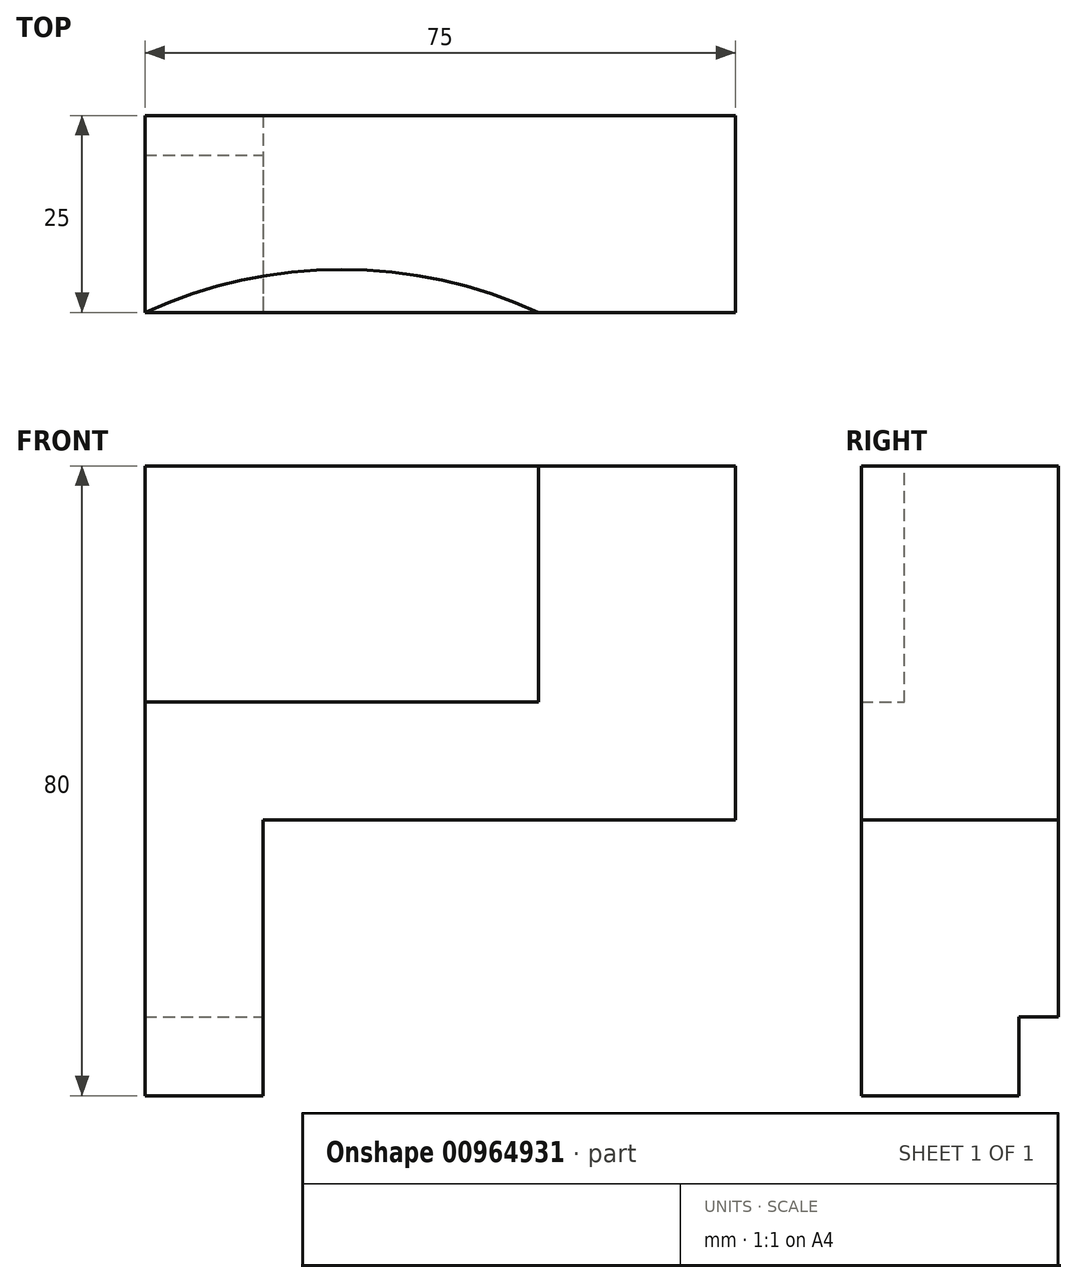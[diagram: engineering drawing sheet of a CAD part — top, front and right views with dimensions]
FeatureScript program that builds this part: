
annotation { "Feature Type Name" : "Feature", "Feature Type Description" : "" }
export const myFeature = defineFeature(function(context is Context, id is Id, definition is map)
    precondition{}
    {
        {
            var Q0;
            Q0=qCreatedBy(makeId("Front.planeOp"),FACE);
            var sketch = newSketch(context, id + "F0", { "sketchPlane" : qUnion([Q0])});
            skLineSegment(sketch, "E0.bottom", {"start": v(0, 0) * mm, "end": v(15, 0) * mm});
            skLineSegment(sketch, "E0.top", {"start": v(0, 80) * mm, "end": v(75, 80) * mm});
            skLineSegment(sketch, "E0.left", {"start": v(0, 0) * mm, "end": v(0, 80) * mm});
            skLineSegment(sketch, "E0.right", {"start": v(75, 35) * mm, "end": v(75, 80) * mm});
            skLineSegment(sketch, "E1.bottom", {"start": v(75, 35) * mm, "end": v(15, 35) * mm});
            skLineSegment(sketch, "E1.right", {"start": v(15, 35) * mm, "end": v(15, 0) * mm});
            skSolve(sketch);
        }
        {
            var Q0;
            Q0 = qSketchRegion(id + "F0", true);
            extrude(context, id + "F1", {"entities" : qUnion([Q0]), "oppositeDirection" : true, "depth" : 25 * mm, "offsetDistance" : 25 * mm});
        }
        {
            var Q0;
            Q0=makeQuery(id+"F1.opExtrude","SWEPT_FACE",FACE,{"disambiguationData":[OSD([sQuery(id+"F0.wireOp",EDGE,"E0.top")])]});
            var sketch = newSketch(context, id + "F2", { "sketchPlane" : qUnion([Q0])});
            skLineSegment(sketch, "E2", {"start": v(0, 0) * mm, "end": v(50, 0) * mm});
            skArc(sketch, "E3", {"start": v(50, 0) * mm, "mid": v(25, 5.46) * mm, "end": v(0, 0) * mm});
            skSolve(sketch);
        }
        {
            var Q0;
            Q0 = qSketchRegion(id + "F2", true);
            extrude(context, id + "F3", {"entities" : qUnion([Q0]), "operationType" : NewBodyOperationType.REMOVE, "oppositeDirection" : true, "depth" : 30 * mm, "offsetDistance" : 25 * mm});
        }
        {
            var Q0;
            Q0=makeQuery(id+"F1.opExtrude","SWEPT_FACE",FACE,{"disambiguationData":[OSD([sQuery(id+"F0.wireOp",EDGE,"E1.right")])]});
            var sketch = newSketch(context, id + "F4", { "sketchPlane" : qUnion([Q0])});
            skLineSegment(sketch, "E4.bottom", {"start": v(25, 0) * mm, "end": v(20, 0) * mm});
            skLineSegment(sketch, "E4.top", {"start": v(25, 10) * mm, "end": v(20, 10) * mm});
            skLineSegment(sketch, "E4.left", {"start": v(25, 0) * mm, "end": v(25, 10) * mm});
            skLineSegment(sketch, "E4.right", {"start": v(20, 0) * mm, "end": v(20, 10) * mm});
            skSolve(sketch);
        }
        {
            var Q0;
            Q0 = qSketchRegion(id + "F4", true);
            extrude(context, id + "F5", {"entities" : qUnion([Q0]), "operationType" : NewBodyOperationType.REMOVE, "endBound" : BoundingType.THROUGH_ALL, "oppositeDirection" : true, "depth" : 25 * mm, "offsetDistance" : 25 * mm});
        }
    });
